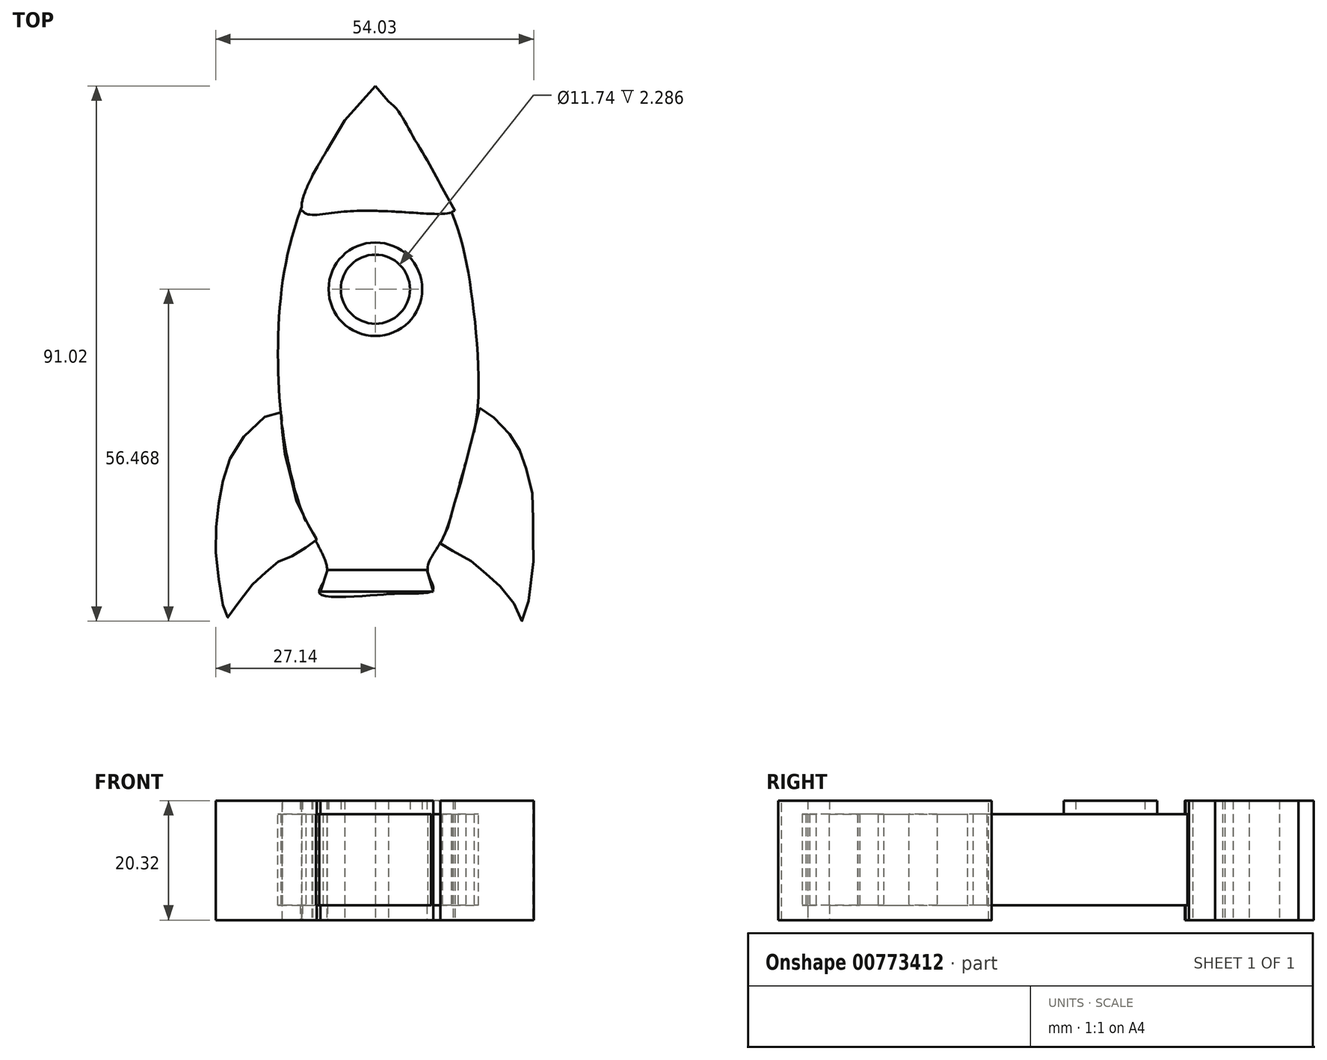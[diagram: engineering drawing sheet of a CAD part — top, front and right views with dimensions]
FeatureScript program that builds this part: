
annotation { "Feature Type Name" : "Feature", "Feature Type Description" : "" }
export const myFeature = defineFeature(function(context is Context, id is Id, definition is map)
    precondition{}
    {
        {
            var Q0;
            Q0=qCreatedBy(makeId("Top.planeOp"),FACE);
            var sketch = newSketch(context, id + "F0", { "sketchPlane" : qUnion([Q0])});
            skFitSpline(sketch, "E0", {"points": [v(-10.38, -25.42) * mm, v(-13.08, -19.1) * mm, v(-15.19, -10.38) * mm, v(-16.4, 0) * mm, v(-16.1, 15.5) * mm, v(-12.78, 30.23) * mm, v(-5.56, 44.67) * mm, v(0, 49.48) * mm, v(4.66, 45.27) * mm, v(12.78, 30.53) * mm, v(16.4, 15.8) * mm, v(17.3, -4.06) * mm, v(14.59, -15.19) * mm, v(11.28, -25.72) * mm, v(8.87, -30.83) * mm, v(9.78, -34.14) * mm, v(6.17, -34.74) * mm, v(0, -35.04) * mm, v(-9.47, -34.74) * mm, v(-8.27, -31.73) * mm, v(-10.38, -25.42) * mm]});
            skSolve(sketch);
        }
        {
            var Q0;
            Q0 = qSketchRegion(id + "F0", true);
            extrude(context, id + "F1", {"entities" : qUnion([Q0]), "depth" : 15.5 * mm, "offsetDistance" : 25.4 * mm});
        }
        {
            var Q0;
            Q0=qCreatedBy(makeId("Top.planeOp"),FACE);
            var sketch = newSketch(context, id + "F2", { "sketchPlane" : qUnion([Q0])});
            skFitSpline(sketch, "E1", {"points": [v(-12.4, 30.4) * mm, v(-6.68, 30.03) * mm, v(5.48, 30.03) * mm, v(13.17, 30.21) * mm, v(12.64, 31.82) * mm, v(9.78, 37.19) * mm, v(6.02, 43.63) * mm, v(3.16, 48.1) * mm, v(0, 49.53) * mm, v(-3.46, 47.38) * mm, v(-7.57, 41.66) * mm, v(-12.4, 30.4) * mm]});
            skSolve(sketch);
        }
        {
            var Q0;
            Q0 = qSketchRegion(id + "F2", true);
            extrude(context, id + "F3", {"entities" : qUnion([Q0]), "operationType" : NewBodyOperationType.ADD, "depth" : 17.78 * mm, "offsetDistance" : 25.4 * mm, "hasSecondDirection" : true, "secondDirectionOppositeDirection" : true, "secondDirectionDepth" : 2.54 * mm});
        }
        {
            var Q0;
            Q0=qCreatedBy(makeId("Top.planeOp"),FACE);
            var sketch = newSketch(context, id + "F4", { "sketchPlane" : qUnion([Q0])});
            skCircle(sketch, "E2", {"center": v(0, 16.98) * mm, "radius": 7.95 * mm});
            skCircle(sketch, "E3", {"center": v(0, 16.98) * mm, "radius": 5.87 * mm});
            skSolve(sketch);
        }
        {
            var Q0;
            Q0 = qSketchRegion(id + "F4", true);
            extrude(context, id + "F5", {"entities" : qUnion([Q0]), "operationType" : NewBodyOperationType.ADD, "depth" : 17.78 * mm, "offsetDistance" : 25.4 * mm});
        }
        {
            var Q0;
            Q0=qCreatedBy(makeId("Top.planeOp"),FACE);
            var sketch = newSketch(context, id + "F6", { "sketchPlane" : qUnion([Q0])});
            skFitSpline(sketch, "E4", {"points": [v(-9.97, -25.63) * mm, v(-11.62, -26.84) * mm, v(-14.33, -28.5) * mm, v(-16.74, -29.54) * mm, v(-19.3, -31.8) * mm, v(-22.45, -35.1) * mm, v(-25.16, -38.87) * mm, v(-26.06, -35.86) * mm, v(-27.12, -27.29) * mm, v(-26.66, -20.07) * mm, v(-25.46, -13.9) * mm, v(-21.55, -7.13) * mm, v(-16.29, -3.83) * mm, v(-15.84, -8.19) * mm, v(-14.63, -13.9) * mm, v(-12.38, -21.57) * mm, v(-9.97, -25.63) * mm]});
            skFitSpline(sketch, "E5", {"points": [v(17.7, -3.22) * mm, v(20.4, -5.18) * mm, v(23.72, -8.94) * mm, v(25.22, -12.25) * mm, v(26.73, -18.41) * mm, v(26.73, -24.43) * mm, v(26.88, -28.34) * mm, v(25.07, -39.47) * mm, v(23.72, -36.76) * mm, v(20.56, -33) * mm, v(17.7, -30.45) * mm, v(14.1, -27.89) * mm, v(11.08, -26.54) * mm, v(11.84, -24.73) * mm, v(13.64, -18.56) * mm, v(14.84, -14.8) * mm, v(15.9, -10.3) * mm, v(17.1, -5.78) * mm, v(17.7, -3.22) * mm]});
            skSolve(sketch);
        }
        {
            var Q0;
            Q0 = qSketchRegion(id + "F6", true);
            extrude(context, id + "F7", {"entities" : qUnion([Q0]), "operationType" : NewBodyOperationType.ADD, "depth" : 17.78 * mm, "offsetDistance" : 25.4 * mm, "hasSecondDirection" : true, "secondDirectionOppositeDirection" : true, "secondDirectionDepth" : 2.54 * mm});
        }
        {
            var Q0;
            Q0=qCreatedBy(makeId("Top.planeOp"),FACE);
            var sketch = newSketch(context, id + "F8", { "sketchPlane" : qUnion([Q0])});
            skLineSegment(sketch, "E6", {"start": v(-8.15, -30.75) * mm, "end": v(-9.3, -34.44) * mm});
            skLineSegment(sketch, "E7", {"start": v(-9.3, -34.44) * mm, "end": v(9.86, -34.44) * mm});
            skLineSegment(sketch, "E8", {"start": v(9.86, -34.44) * mm, "end": v(8.78, -30.75) * mm});
            skLineSegment(sketch, "E9", {"start": v(8.78, -30.75) * mm, "end": v(-8.15, -30.75) * mm});
            skLineSegment(sketch, "E10", {"start": v(-12.75, 30.3) * mm, "end": v(-10.68, 36.39) * mm});
            skLineSegment(sketch, "E11", {"start": v(-10.68, 36.39) * mm, "end": v(-5.24, 45.7) * mm});
            skLineSegment(sketch, "E12", {"start": v(-5.24, 45.7) * mm, "end": v(0, 51.53) * mm});
            skLineSegment(sketch, "E13", {"start": v(0, 51.53) * mm, "end": v(4.85, 45.7) * mm});
            skLineSegment(sketch, "E14", {"start": v(4.85, 45.7) * mm, "end": v(10.16, 36.39) * mm});
            skLineSegment(sketch, "E15", {"start": v(10.16, 36.39) * mm, "end": v(13.53, 30.3) * mm});
            skLineSegment(sketch, "E16", {"start": v(13.53, 30.3) * mm, "end": v(-12.75, 30.3) * mm});
            skSolve(sketch);
        }
        {
            var Q0;
            Q0 = qSketchRegion(id + "F8", true);
            extrude(context, id + "F9", {"entities" : qUnion([Q0]), "operationType" : NewBodyOperationType.ADD, "depth" : 17.78 * mm, "offsetDistance" : 25.4 * mm, "hasSecondDirection" : true, "secondDirectionOppositeDirection" : true, "secondDirectionDepth" : 2.54 * mm});
        }
    });
